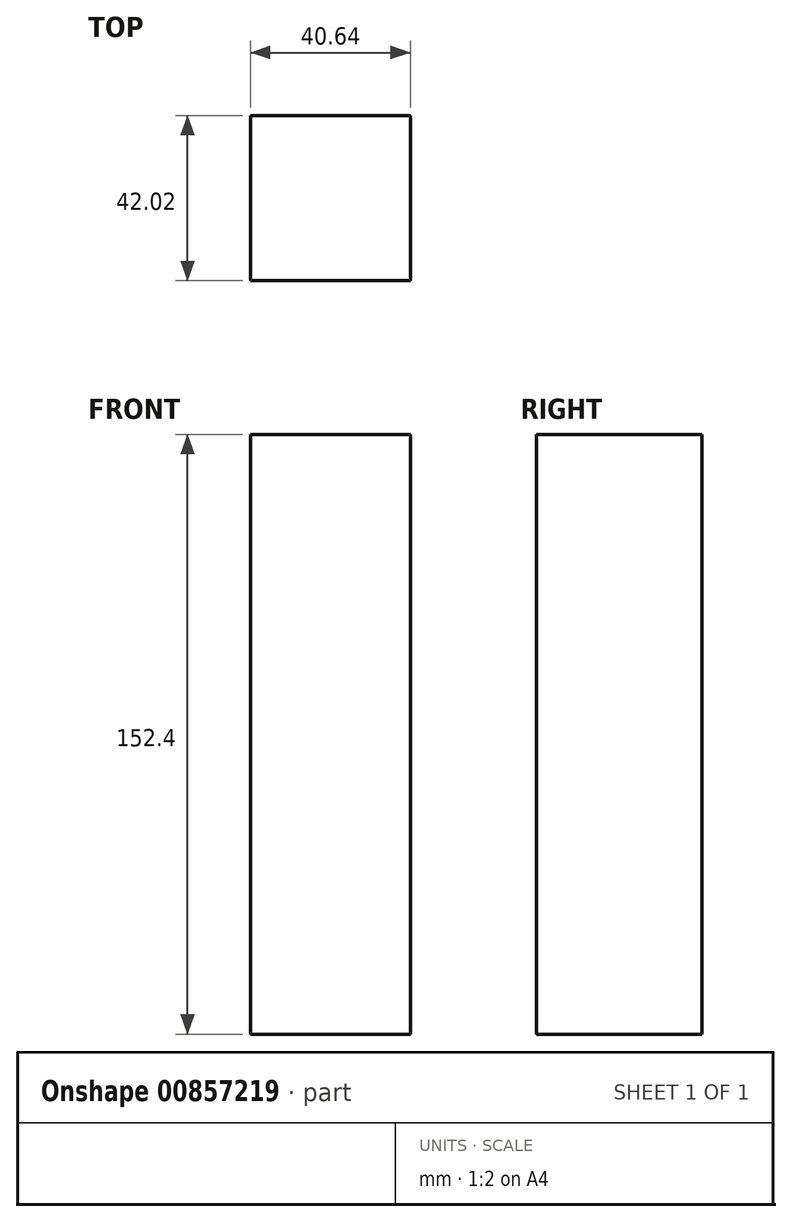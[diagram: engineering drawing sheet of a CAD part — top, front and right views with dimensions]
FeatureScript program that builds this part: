
annotation { "Feature Type Name" : "Feature", "Feature Type Description" : "" }
export const myFeature = defineFeature(function(context is Context, id is Id, definition is map)
    precondition{}
    {
        {
            var Q0;
            Q0=qCreatedBy(makeId("Top.planeOp"),FACE);
            var sketch = newSketch(context, id + "F0", { "sketchPlane" : qUnion([Q0])});
            skLineSegment(sketch, "E0.bottom", {"start": v(20.32, -21.01) * mm, "end": v(-20.32, -21.01) * mm});
            skLineSegment(sketch, "E0.top", {"start": v(20.32, 21.01) * mm, "end": v(-20.32, 21.01) * mm});
            skLineSegment(sketch, "E0.left", {"start": v(20.32, -21.01) * mm, "end": v(20.32, 21.01) * mm});
            skLineSegment(sketch, "E0.right", {"start": v(-20.32, -21.01) * mm, "end": v(-20.32, 21.01) * mm});
            skPoint(sketch, "E0.middle", {"position": v(0, 0) * mm});
            skLineSegment(sketch, "E1.bottom", {"start": v(82.3, -47.62) * mm, "end": v(-82.3, -47.62) * mm});
            skLineSegment(sketch, "E1.top", {"start": v(82.3, 47.62) * mm, "end": v(-82.3, 47.62) * mm});
            skLineSegment(sketch, "E1.left", {"start": v(82.3, -47.62) * mm, "end": v(82.3, 47.62) * mm});
            skLineSegment(sketch, "E1.right", {"start": v(-82.3, -47.62) * mm, "end": v(-82.3, 47.62) * mm});
            skSolve(sketch);
        }
        {
            var Q0;
            Q0=sQuery(id+"F0.wireOp",EDGE,"E1.right");
            extrude(context, id + "F1", {"bodyType" : ToolBodyType.SURFACE, "surfaceEntities" : qUnion([Q0]), "depth" : 25.4 * mm, "offsetDistance" : 25.4 * mm});
        }
        {
            var Q0;
            Q0=sQuery(id+"F0.wireOp",EDGE,"E1.bottom");
            extrude(context, id + "F2", {"bodyType" : ToolBodyType.SURFACE, "surfaceEntities" : qUnion([Q0]), "depth" : 25.4 * mm, "offsetDistance" : 25.4 * mm});
        }
        {
            var Q0;
            Q0=sQuery(id+"F0.wireOp",EDGE,"E1.left");
            extrude(context, id + "F3", {"bodyType" : ToolBodyType.SURFACE, "surfaceEntities" : qUnion([Q0]), "depth" : 25.4 * mm, "offsetDistance" : 25.4 * mm});
        }
        {
            var Q0;
            Q0=sQuery(id+"F0.wireOp",EDGE,"E1.top");
            extrude(context, id + "F4", {"bodyType" : ToolBodyType.SURFACE, "surfaceEntities" : qUnion([Q0]), "depth" : 25.4 * mm, "offsetDistance" : 25.4 * mm});
        }
        {
            var Q0;
            Q0=makeQuery(id+"F0.imprint","IMPRINT",FACE,{"disambiguationData":[TD([[makeQuery(id+"F0.imprint","IMPRINT",EDGE,{"derivedFrom":sQuery(id+"F0.wireOp",EDGE,"E0.bottom")}),-1.0]])]});
            extrude(context, id + "F5", {"entities" : qUnion([Q0]), "depth" : 152.4 * mm, "offsetDistance" : 25.4 * mm});
        }
    });
